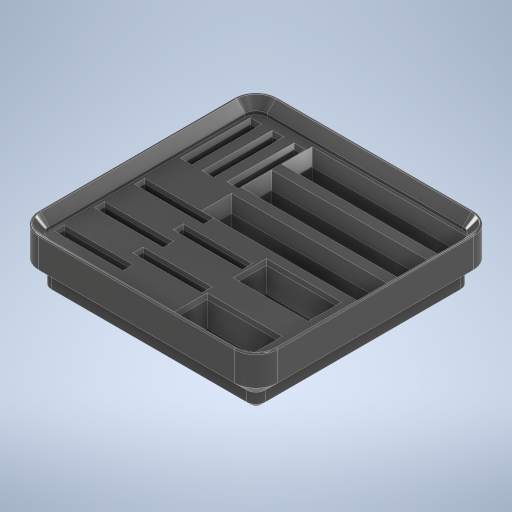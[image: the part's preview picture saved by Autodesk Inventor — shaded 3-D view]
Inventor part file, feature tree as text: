
AUTODESK INVENTOR PART (.ipt)
format: ipt  version: 2023 (Build 270158030, 158C)  size: 656,896 bytes
history: native  units: mm
features: extrude x11, sketch x10, chamfer x6, projected_geometry x6, fillet x1, pattern_linear x1
ambient origin geometry x8: Origin, YZ Plane, XZ Plane, XY Plane, X Axis, Y Axis, Z Axis, Center Point
bodies: Solid2 (feature_tree)
feature tree (35):
  extrude  "base-generic"  Depth=41.5mm
  extrude  "Extrusion8"  Depth=3.75mm TaperAngle=0.0deg
  extrude  "Extrusion9"  Depth=2.15mm
  extrude  "Extrusion10"  Depth=1.8mm
  extrude  "Extrusion11"  Depth=7.75mm
  extrude  "Extrusion12"  Depth=7.75mm
  extrude  "Extrusion15"  Depth=2.4mm TaperAngle=0.0deg
  chamfer  "Chamfer5"  Distance=6.0mm
  fillet  "Fillet4"  Radius=3.75mm
  extrude  "Extrusion16"  Depth=1.8mm
  sketch  "Sketch19"  dims[d79=2.25mm d80=0.0mm d84=1.8mm d85=5.4mm d86=0.0mm d94=1.8mm d95=2.0mm d96=45.0deg d97=0.2mm d98=2.3mm d99=0.0mm d100=4.8mm d101=4.8mm d102=12.1mm d106=1.0mm d109=2.25mm d110=24.2mm d126=3.0mm d127=0.0mm d128=0.4mm d129=2.0mm d130=45.0deg d131=1.8mm d132=0.0mm d134=1.0mm d135=5.5mm d137=0.4mm d138=2.0mm d139=45.0deg d143=0.5mm d144=2.0mm d145=45.0deg d149=1.5mm d150=2.0mm d151=45.0deg d155=30.0mm d157=7.0mm d158=10.0mm d160=10.0mm d162=30.0mm d164=7.0mm d165=10.0mm d167=10.0mm d169=11.2mm d170=1.0mm d171=2.5mm d172=2.5mm d173=20.0mm d175=7.0mm d176=10.0mm d178=10.0mm d181=7.0mm d182=11.2mm d183=11.2mm d184=2.0mm d185=30.0mm d187=3.8mm d188=10.0mm d190=10.0mm d192=0.5mm d193=2.0mm d194=45.0deg d196=1.0mm d197=1.0mm d198=1.0mm d17=0.5mm d18=0.872665mm d19=0.5mm d20=0.872665mm d24=0.0mm d25=0.0mm d26=0.0mm d27=0.0mm d152=0.0mm d153=0.0mm d154=0.0mm]
  extrude  "Extrusion17"  Depth=0.5mm TaperAngle=0.0deg
  chamfer  "Chamfer6"  Distance=1.8mm Angle=45.0deg
  extrude  "Extrusion18"  Depth=0.2mm
  chamfer  "Chamfer7"  Distance=2.3mm
  chamfer  "Chamfer9"  Distance=4.8mm
  chamfer  "Chamfer11"  Distance=4.8mm
  chamfer  "Chamfer13"  Distance=12.1mm
  pattern_linear  "Rectangular Pattern1"  Spacing1=1.0mm  [1 undecoded]
  extrude  "Extrusion13"  Depth=2.25mm
  sketch  "Sketch9"  dims[d50=41.5mm d51=41.5mm]
  sketch  "Sketch10"  dims[d52=3.75mm d53=0.1mm d54=0.0mm]
  projected_geometry  "Projected Loop2"
  sketch  "Sketch11"  dims[d55=3.75mm d56=2.15mm d57=-7.853982mm]
  projected_geometry  "Projected Loop3"
  sketch  "Sketch12"  dims[d58=1.8mm d59=0.0mm d60=0.8mm d61=-7.853982mm]
  projected_geometry  "Projected Loop4"
  sketch  "Sketch13"  dims[d62=6.5mm d63=7.75mm]
  sketch  "Sketch14"  dims[d64=7.75mm d65=7.75mm]
  sketch  "Sketch15"  dims[d66=7.75mm d67=2.4mm d68=0.0mm]
  sketch  "Sketch17"  dims[d69=3.0mm d70=6.0mm d71=0.0mm]
  projected_geometry  "Projected Loop6"
  sketch  "Sketch18"  dims[d72=20.0mm d74=42.0mm d75=20.0mm d77=42.0mm d78=3.75mm]
  projected_geometry  "Projected Loop7"
  projected_geometry  "Projected Loop9"
note: 1 required parameter value undecoded (feature->parameter linkage not recoverable at this tier; creation-order binding heuristic only, values carry confidence <= 0.55)
